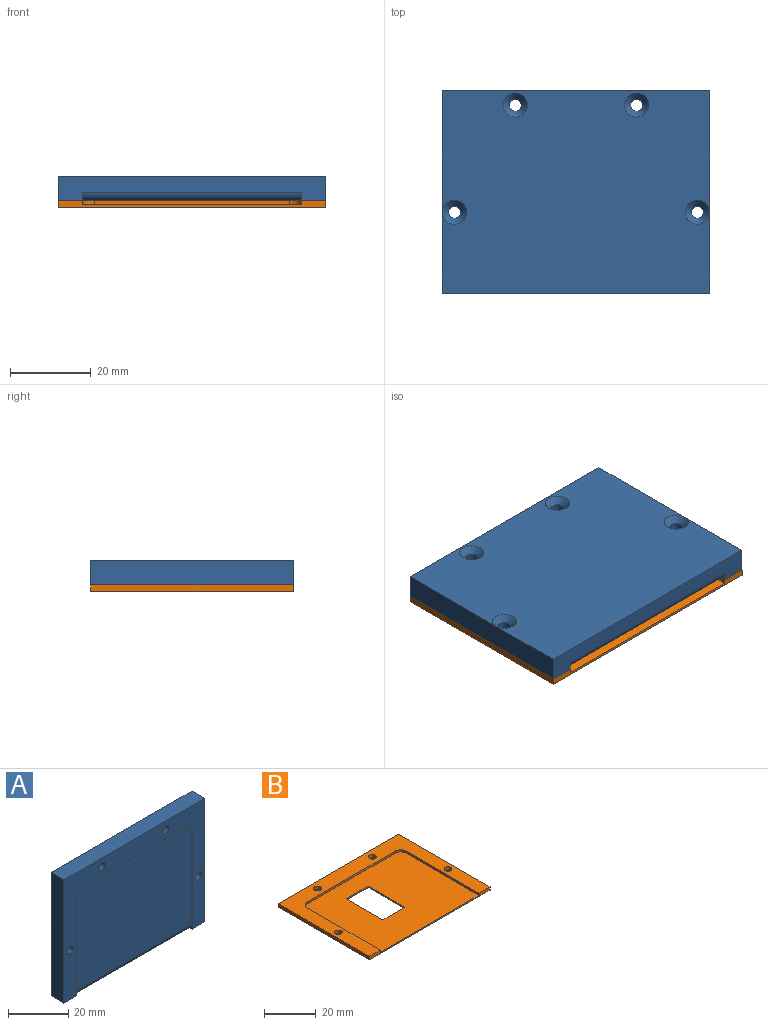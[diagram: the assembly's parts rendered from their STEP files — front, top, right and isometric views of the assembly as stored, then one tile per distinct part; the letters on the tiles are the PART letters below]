
ASSEMBLY  parts=2 mates=1
PART A: 21 faces, bbox 66x6x50 mm
  f0: plane 39.88x2.1mm, normal (1,0,0), area 4.8mm2, adj f1,f5,f13,f15,f16
  f1: cylinder r=3mm len=3mm, axis (0,1,0), area 0.5mm2, adj f0,f2,f13,f15
  f2: plane 48x0.1mm, normal (0,0,-1), area 4.8mm2, adj f1,f3,f13,f15
  f3: cylinder r=3mm len=3mm, axis (0,1,0), area 0.5mm2, adj f2,f4,f13,f15
  f4: plane 39.88x2.1mm, normal (-1,0,0), area 4.8mm2, adj f3,f5,f13,f15,f16
  f5: plane 66x6mm, normal (0,0,-1), area 282.6mm2, adj f0,f4,f6,f12,f13,f14,f16
  f6: plane 50x6mm, normal (1,0,0), area 300mm2, adj f5,f7,f13,f14
  f7: plane 66x6mm, normal (0,0,1), area 396mm2, adj f6,f12,f13,f14
  f8: cylinder r=1.51mm len=4.5mm, axis (0,1,0), area 42.6mm2, adj f13,f18
  f9: cylinder r=1.51mm len=4.5mm, axis (0,1,0), area 42.6mm2, adj f13,f20
  f10: cylinder r=1.5mm len=4.5mm, axis (0,1,0), area 42.4mm2, adj f13,f19
  f11: cylinder r=1.5mm len=4.5mm, axis (0,1,0), area 42.4mm2, adj f13,f17
  f12: plane 50x6mm, normal (-1,0,0), area 300mm2, adj f5,f7,f13,f14
  f13: plane 66x50mm, normal (0,-1,0), area 960.2mm2, adj f0,f1,f2,f3,f4,f5,f6,f7
  f14: plane 66x50mm, normal (0,1,0), area 3186.7mm2, adj f5,f6,f7,f12,f17,f18,f19,f20
  f15: plane 54x40.88mm, normal (0,-1,0), area 2203.4mm2, adj f0,f1,f2,f3,f4,f16
  f16: cylinder r=2mm len=54mm, axis (-1,0,0), area 169.6mm2, adj f0,f4,f5,f15
  f17: cone r=3mm half-angle=45deg, axis (0,1,0), area 30mm2, adj f11,f14
  f18: cone r=3mm half-angle=45deg, axis (0,1,0), area 30.1mm2, adj f8,f14
  f19: cone r=3mm half-angle=45deg, axis (0,1,0), area 30mm2, adj f10,f14
  f20: cone r=3mm half-angle=45deg, axis (0,1,0), area 30.1mm2, adj f9,f14
PART B: 20 faces, bbox 66x50x1.6 mm
  f0: plane 39.88x1mm, normal (1,0,0), area 39.9mm2, adj f1,f5,f13,f19
  f1: cylinder r=3mm len=3mm, axis (0,0,-1), area 4.7mm2, adj f0,f2,f13,f19
  f2: plane 48x1mm, normal (0,-1,0), area 48mm2, adj f1,f3,f13,f19
  f3: cylinder r=3mm len=3mm, axis (0,0,-1), area 4.7mm2, adj f2,f4,f13,f19
  f4: plane 39.88x1mm, normal (-1,0,0), area 39.9mm2, adj f3,f5,f13,f19
  f5: plane 66x1.6mm, normal (0,-1,0), area 51.6mm2, adj f0,f4,f6,f12,f13,f14,f19
  f6: plane 50x1.6mm, normal (1,0,0), area 80mm2, adj f5,f7,f13,f14
  f7: plane 66x1.6mm, normal (0,1,0), area 105.6mm2, adj f6,f12,f13,f14
  f8: cylinder r=1.51mm len=3.01mm, axis (0,0,-1), area 15.1mm2, adj f13,f14
  f9: cylinder r=1.51mm len=3.01mm, axis (0,0,-1), area 15.1mm2, adj f13,f14
  f10: cylinder r=1.5mm len=3mm, axis (0,0,-1), area 15.1mm2, adj f13,f14
  f11: cylinder r=1.5mm len=3mm, axis (0,0,-1), area 15.1mm2, adj f13,f14
  f12: plane 50x1.6mm, normal (-1,0,0), area 80mm2, adj f5,f7,f13,f14
  f13: plane 66x50mm, normal (0,0,1), area 960.2mm2, adj f0,f1,f2,f3,f4,f5,f6,f7
  f14: plane 66x50mm, normal (0,0,-1), area 3031.6mm2, adj f5,f6,f7,f8,f9,f10,f11,f12
  f15: plane 20x0.6mm, normal (-1,0,0), area 12mm2, adj f14,f16,f18,f19
  f16: plane 12x0.6mm, normal (0,1,0), area 7.2mm2, adj f14,f15,f17,f19
  f17: plane 20x0.6mm, normal (1,0,0), area 12mm2, adj f14,f16,f18,f19
  f18: plane 12x0.6mm, normal (0,-1,0), area 7.2mm2, adj f14,f15,f17,f19
  f19: plane 54x42.88mm, normal (0,0,1), area 2071.4mm2, adj f0,f1,f2,f3,f4,f5,f15,f16
PLACE A rot(axis=(0,0.71,0.71),180deg) t=(22.12,-32.64,39.39)mm
PLACE B rot(axis=(-0.05,-0.06,-1),0deg) t=(22.12,-32.64,32.39)mm
MATE fastened B.f8 <-> A.f9  axis (0,0,1) through (7.12,13.8,33.39)mm
